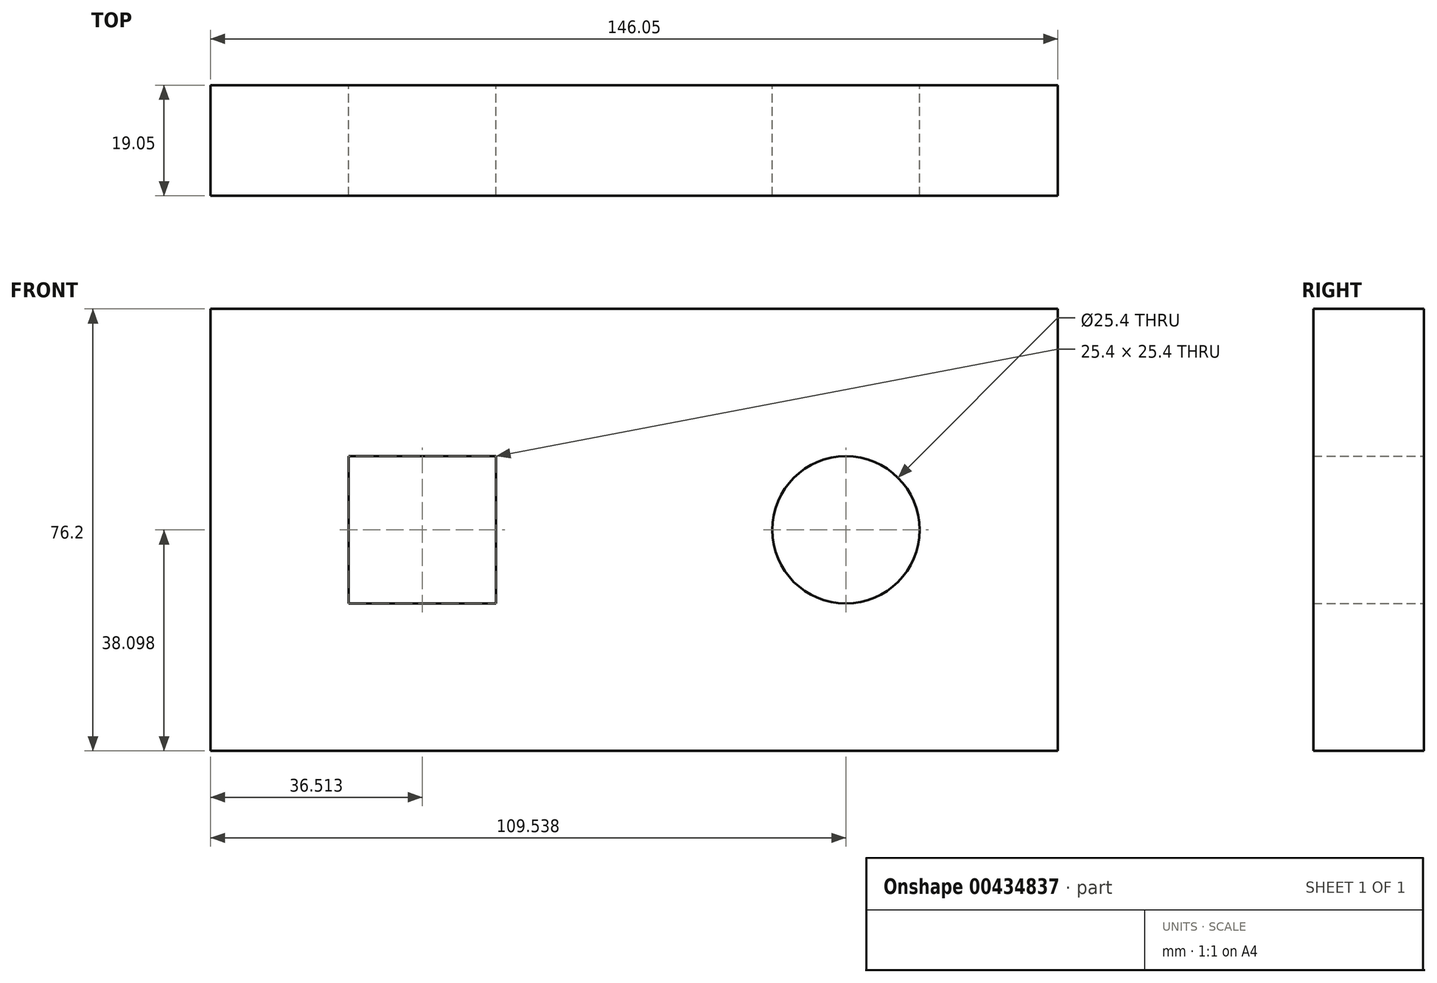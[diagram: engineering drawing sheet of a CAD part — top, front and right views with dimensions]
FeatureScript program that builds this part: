
annotation { "Feature Type Name" : "Feature", "Feature Type Description" : "" }
export const myFeature = defineFeature(function(context is Context, id is Id, definition is map)
    precondition{}
    {
        {
            var Q0;
            Q0=qCreatedBy(makeId("Front.planeOp"),FACE);
            var sketch = newSketch(context, id + "F0", { "sketchPlane" : qUnion([Q0])});
            skLineSegment(sketch, "E0.bottom", {"start": v(-73.87, 41.83) * mm, "end": v(72.18, 41.83) * mm});
            skLineSegment(sketch, "E0.top", {"start": v(-73.87, -34.37) * mm, "end": v(72.18, -34.37) * mm});
            skLineSegment(sketch, "E0.left", {"start": v(-73.87, 41.83) * mm, "end": v(-73.87, -34.37) * mm});
            skLineSegment(sketch, "E0.right", {"start": v(72.18, 41.83) * mm, "end": v(72.18, -34.37) * mm});
            skLineSegment(sketch, "E1.bottom", {"start": v(-50.06, 16.43) * mm, "end": v(-24.66, 16.43) * mm});
            skLineSegment(sketch, "E1.top", {"start": v(-50.06, -8.97) * mm, "end": v(-24.66, -8.97) * mm});
            skLineSegment(sketch, "E1.left", {"start": v(-50.06, 16.43) * mm, "end": v(-50.06, -8.97) * mm});
            skLineSegment(sketch, "E1.right", {"start": v(-24.66, 16.43) * mm, "end": v(-24.66, -8.97) * mm});
            skCircle(sketch, "E2", {"center": v(35.67, 3.73) * mm, "radius": 12.7 * mm});
            skSolve(sketch);
        }
        {
            var Q0;
            Q0 = qSketchRegion(id + "F0", true);
            extrude(context, id + "F1", {"entities" : qUnion([Q0]), "depth" : 19.05 * mm});
        }
    });
